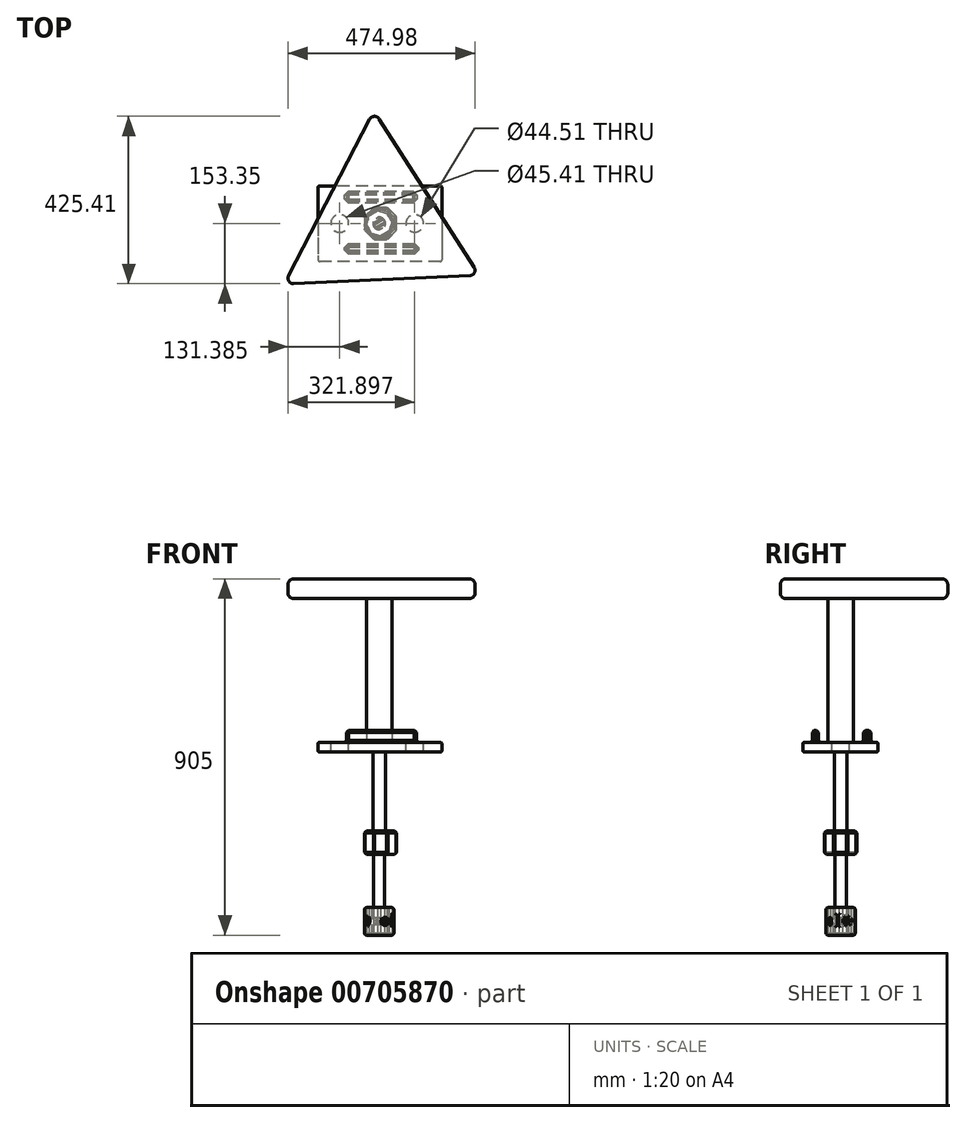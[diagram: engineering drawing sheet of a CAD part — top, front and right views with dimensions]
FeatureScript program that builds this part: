
annotation { "Feature Type Name" : "Feature", "Feature Type Description" : "" }
export const myFeature = defineFeature(function(context is Context, id is Id, definition is map)
    precondition{}
    {
        {
            var Q0;
            Q0=qCreatedBy(makeId("Top.planeOp"),FACE);
            var sketch = newSketch(context, id + "F0", { "sketchPlane" : qUnion([Q0])});
            skCircle(sketch, "E0.cCircle", {"center": v(0, 0) * mm, "radius": 34.9 * mm, "construction": true});
            skLineSegment(sketch, "E0.0", {"start": v(23.22, 29.8) * mm, "end": v(37.49, 4.65) * mm});
            skLineSegment(sketch, "E0.1", {"start": v(37.49, 4.65) * mm, "end": v(29.8, -23.22) * mm});
            skLineSegment(sketch, "E0.2", {"start": v(29.8, -23.22) * mm, "end": v(4.65, -37.49) * mm});
            skLineSegment(sketch, "E0.3", {"start": v(4.65, -37.49) * mm, "end": v(-23.22, -29.8) * mm});
            skLineSegment(sketch, "E0.4", {"start": v(-23.22, -29.8) * mm, "end": v(-37.49, -4.65) * mm});
            skLineSegment(sketch, "E0.5", {"start": v(-37.49, -4.65) * mm, "end": v(-29.8, 23.22) * mm});
            skLineSegment(sketch, "E0.6", {"start": v(-29.8, 23.22) * mm, "end": v(-4.65, 37.49) * mm});
            skLineSegment(sketch, "E0.7", {"start": v(-4.65, 37.49) * mm, "end": v(23.22, 29.8) * mm});
            skPoint(sketch, "E0.0.midPoint", {"position": v(30.35, 17.23) * mm});
            skSolve(sketch);
        }
        {
            var Q0;
            Q0 = qSketchRegion(id + "F0", true);
            extrude(context, id + "F1", {"entities" : qUnion([Q0]), "depth" : 70 * mm, "offsetDistance" : 25 * mm});
        }
        {
            var Q0;
            Q0=makeQuery(id+"F1.opExtrude","CAP_FACE",FACE,{"disambiguationData":[OSD([sQuery(id+"F0.wireOp",EDGE,"E0.0"),sQuery(id+"F0.wireOp",EDGE,"E0.1"),sQuery(id+"F0.wireOp",EDGE,"E0.2"),sQuery(id+"F0.wireOp",EDGE,"E0.3"),sQuery(id+"F0.wireOp",EDGE,"E0.4"),sQuery(id+"F0.wireOp",EDGE,"E0.5"),sQuery(id+"F0.wireOp",EDGE,"E0.6"),sQuery(id+"F0.wireOp",EDGE,"E0.7")])],"isStart":false});
            shell(context, id + "F2", {"entities" : qUnion([Q0]), "thickness" : 5 * mm});
        }
        {
            var Q0;
            Q0=makeQuery(id+"F1.opExtrude","SWEPT_FACE",FACE,{"disambiguationData":[OSD([sQuery(id+"F0.wireOp",EDGE,"E0.2")])]});
            var sketch = newSketch(context, id + "F3", { "sketchPlane" : qUnion([Q0])});
            skCircle(sketch, "E1", {"center": v(0, 34.96) * mm, "radius": 10.52 * mm});
            skSolve(sketch);
        }
        {
            var Q0;
            Q0 = qSketchRegion(id + "F3", true);
            extrude(context, id + "F4", {"entities" : qUnion([Q0]), "operationType" : NewBodyOperationType.REMOVE, "oppositeDirection" : true, "depth" : 72.7 * mm, "offsetDistance" : 25 * mm});
        }
        {
            var Q0;
            Q0=makeQuery(id+"F1.opExtrude","SWEPT_FACE",FACE,{"disambiguationData":[OSD([sQuery(id+"F0.wireOp",EDGE,"E0.1")])]});
            var sketch = newSketch(context, id + "F5", { "sketchPlane" : qUnion([Q0])});
            skLineSegment(sketch, "E2.bottom", {"start": v(0, 25.22) * mm, "end": v(2.73, 25.22) * mm});
            skLineSegment(sketch, "E2.top", {"start": v(0, 49.95) * mm, "end": v(2.73, 49.95) * mm});
            skLineSegment(sketch, "E2.left", {"start": v(0, 25.22) * mm, "end": v(0, 49.95) * mm});
            skLineSegment(sketch, "E2.right", {"start": v(2.73, 25.22) * mm, "end": v(2.73, 49.95) * mm});
            skSolve(sketch);
        }
        {
            var Q0;
            Q0 = qSketchRegion(id + "F5", true);
            extrude(context, id + "F6", {"entities" : qUnion([Q0]), "operationType" : NewBodyOperationType.REMOVE, "oppositeDirection" : true, "depth" : 81.6 * mm, "offsetDistance" : 25 * mm});
        }
        {
            var Q0;
            Q0=makeQuery(id+"F2.opShell","OFFSET_FACE",FACE,{"disambiguationData":[OSD([sQuery(id+"F0.wireOp",EDGE,"E0.0"),sQuery(id+"F0.wireOp",EDGE,"E0.1"),sQuery(id+"F0.wireOp",EDGE,"E0.2"),sQuery(id+"F0.wireOp",EDGE,"E0.3"),sQuery(id+"F0.wireOp",EDGE,"E0.4"),sQuery(id+"F0.wireOp",EDGE,"E0.5"),sQuery(id+"F0.wireOp",EDGE,"E0.6"),sQuery(id+"F0.wireOp",EDGE,"E0.7")])]});
            var sketch = newSketch(context, id + "F7", { "sketchPlane" : qUnion([Q0])});
            skCircle(sketch, "E3", {"center": v(0, 0) * mm, "radius": 14.1 * mm});
            skSolve(sketch);
        }
        {
            var Q0;
            Q0 = qSketchRegion(id + "F7", true);
            extrude(context, id + "F8", {"entities" : qUnion([Q0]), "operationType" : NewBodyOperationType.ADD, "depth" : 200 * mm, "offsetDistance" : 25 * mm});
        }
        {
            var Q0;
            Q0=makeQuery(id+"F1.opExtrude","SWEPT_FACE",FACE,{"disambiguationData":[OSD([sQuery(id+"F0.wireOp",EDGE,"E0.0")])]});
            var sketch = newSketch(context, id + "F9", { "sketchPlane" : qUnion([Q0])});
            skCircle(sketch, "E4.cCircle", {"center": v(0, 36.54) * mm, "radius": 7.96 * mm, "construction": true});
            skLineSegment(sketch, "E4.0", {"start": v(-3.31, 27.96) * mm, "end": v(-9.08, 35.12) * mm});
            skLineSegment(sketch, "E4.1", {"start": v(-9.08, 35.12) * mm, "end": v(-5.77, 43.7) * mm});
            skLineSegment(sketch, "E4.2", {"start": v(-5.77, 43.7) * mm, "end": v(3.31, 45.12) * mm});
            skLineSegment(sketch, "E4.3", {"start": v(3.31, 45.12) * mm, "end": v(9.08, 37.96) * mm});
            skLineSegment(sketch, "E4.4", {"start": v(9.08, 37.96) * mm, "end": v(5.77, 29.39) * mm});
            skLineSegment(sketch, "E4.5", {"start": v(5.77, 29.39) * mm, "end": v(-3.31, 27.96) * mm});
            skPoint(sketch, "E4.0.midPoint", {"position": v(-6.2, 31.54) * mm});
            skSolve(sketch);
        }
        {
            var Q0;
            Q0 = qSketchRegion(id + "F9", true);
            extrude(context, id + "F10", {"entities" : qUnion([Q0]), "operationType" : NewBodyOperationType.REMOVE, "oppositeDirection" : true, "depth" : 96 * mm, "offsetDistance" : 25 * mm});
        }
        {
            var Q0;
            Q0=makeQuery(id+"F8.opExtrude","CAP_FACE",FACE,{"disambiguationData":[OSD([sQuery(id+"F7.wireOp",EDGE,"E3")])],"isStart":false});
            var sketch = newSketch(context, id + "F11", { "sketchPlane" : qUnion([Q0])});
            skCircle(sketch, "E5.cCircle", {"center": v(3.58, 0) * mm, "radius": 40.85 * mm, "construction": true});
            skLineSegment(sketch, "E5.0", {"start": v(20.5, -40.85) * mm, "end": v(-13.34, -40.85) * mm});
            skLineSegment(sketch, "E5.1", {"start": v(-13.34, -40.85) * mm, "end": v(-37.27, -16.92) * mm});
            skLineSegment(sketch, "E5.2", {"start": v(-37.27, -16.92) * mm, "end": v(-37.27, 16.92) * mm});
            skLineSegment(sketch, "E5.3", {"start": v(-37.27, 16.92) * mm, "end": v(-13.34, 40.85) * mm});
            skLineSegment(sketch, "E5.4", {"start": v(-13.34, 40.85) * mm, "end": v(20.5, 40.85) * mm});
            skLineSegment(sketch, "E5.5", {"start": v(20.5, 40.85) * mm, "end": v(44.43, 16.92) * mm});
            skLineSegment(sketch, "E5.6", {"start": v(44.43, 16.92) * mm, "end": v(44.43, -16.92) * mm});
            skLineSegment(sketch, "E5.7", {"start": v(44.43, -16.92) * mm, "end": v(20.5, -40.85) * mm});
            skPoint(sketch, "E5.0.midPoint", {"position": v(3.58, -40.85) * mm});
            skSolve(sketch);
        }
        {
            var Q0;
            Q0 = qSketchRegion(id + "F11", true);
            extrude(context, id + "F12", {"entities" : qUnion([Q0]), "operationType" : NewBodyOperationType.ADD, "depth" : 60 * mm, "offsetDistance" : 25 * mm});
        }
        {
            var Q0;
            Q0=makeQuery(id+"F12.opExtrude","CAP_EDGE",EDGE,{"disambiguationData":[OSD([sQuery(id+"F11.wireOp",EDGE,"E5.7")])],"isStart":false});
            var Q1;
            Q1=makeQuery(id+"F12.opExtrude","CAP_EDGE",EDGE,{"disambiguationData":[OSD([sQuery(id+"F11.wireOp",EDGE,"E5.6")])],"isStart":false});
            var Q2;
            Q2=makeQuery(id+"F12.opExtrude","CAP_EDGE",EDGE,{"disambiguationData":[OSD([sQuery(id+"F11.wireOp",EDGE,"E5.5")])],"isStart":false});
            var Q3;
            Q3=makeQuery(id+"F12.opExtrude","CAP_EDGE",EDGE,{"disambiguationData":[OSD([sQuery(id+"F11.wireOp",EDGE,"E5.4")])],"isStart":false});
            var Q4;
            Q4=makeQuery(id+"F12.opExtrude","CAP_EDGE",EDGE,{"disambiguationData":[OSD([sQuery(id+"F11.wireOp",EDGE,"E5.3")])],"isStart":false});
            var Q5;
            Q5=makeQuery(id+"F12.opExtrude","CAP_EDGE",EDGE,{"disambiguationData":[OSD([sQuery(id+"F11.wireOp",EDGE,"E5.2")])],"isStart":false});
            var Q6;
            Q6=makeQuery(id+"F12.opExtrude","CAP_EDGE",EDGE,{"disambiguationData":[OSD([sQuery(id+"F11.wireOp",EDGE,"E5.1")])],"isStart":false});
            var Q7;
            Q7=makeQuery(id+"F12.opExtrude","CAP_EDGE",EDGE,{"disambiguationData":[OSD([sQuery(id+"F11.wireOp",EDGE,"E5.0")])],"isStart":false});
            var Q8;
            Q8=makeQuery(id+"F12.opExtrude","SWEPT_FACE",FACE,{"disambiguationData":[OSD([sQuery(id+"F11.wireOp",EDGE,"E5.4")])]});
            var Q9;
            Q9=makeQuery(id+"F12.opExtrude","SWEPT_FACE",FACE,{"disambiguationData":[OSD([sQuery(id+"F11.wireOp",EDGE,"E5.3")])]});
            var Q10;
            Q10=makeQuery(id+"F12.opExtrude","SWEPT_FACE",FACE,{"disambiguationData":[OSD([sQuery(id+"F11.wireOp",EDGE,"E5.2")])]});
            var Q11;
            Q11=makeQuery(id+"F12.opExtrude","SWEPT_FACE",FACE,{"disambiguationData":[OSD([sQuery(id+"F11.wireOp",EDGE,"E5.1")])]});
            var Q12;
            Q12=makeQuery(id+"F12.opExtrude","SWEPT_FACE",FACE,{"disambiguationData":[OSD([sQuery(id+"F11.wireOp",EDGE,"E5.0")])]});
            var Q13;
            Q13=makeQuery(id+"F12.opExtrude","SWEPT_FACE",FACE,{"disambiguationData":[OSD([sQuery(id+"F11.wireOp",EDGE,"E5.6")])]});
            chamfer(context, id + "F13", {"entities" : qUnion([Q0, Q1, Q2, Q3, Q4, Q5, Q6, Q7, Q8, Q9, Q10, Q11, Q12, Q13]), "width" : 5 * mm, "tangentPropagation" : true});
        }
        {
            var Q0;
            Q0=makeQuery(id+"F1.opExtrude","SWEPT_FACE",FACE,{"disambiguationData":[OSD([sQuery(id+"F0.wireOp",EDGE,"E0.4")])]});
            var Q1;
            Q1=makeQuery(id+"F1.opExtrude","SWEPT_FACE",FACE,{"disambiguationData":[OSD([sQuery(id+"F0.wireOp",EDGE,"E0.5")])]});
            var Q2;
            Q2=makeQuery(id+"F1.opExtrude","SWEPT_FACE",FACE,{"disambiguationData":[OSD([sQuery(id+"F0.wireOp",EDGE,"E0.6")])]});
            var Q3;
            Q3=makeQuery(id+"F1.opExtrude","SWEPT_FACE",FACE,{"disambiguationData":[OSD([sQuery(id+"F0.wireOp",EDGE,"E0.7")])]});
            var Q4;
            Q4=makeQuery(id+"F1.opExtrude","SWEPT_FACE",FACE,{"disambiguationData":[OSD([sQuery(id+"F0.wireOp",EDGE,"E0.0")])]});
            var Q5;
            Q5=makeQuery(id+"F1.opExtrude","SWEPT_FACE",FACE,{"disambiguationData":[OSD([sQuery(id+"F0.wireOp",EDGE,"E0.1")])]});
            var Q6;
            Q6=makeQuery(id+"F1.opExtrude","SWEPT_FACE",FACE,{"disambiguationData":[OSD([sQuery(id+"F0.wireOp",EDGE,"E0.2")])]});
            var Q7;
            Q7=makeQuery(id+"F1.opExtrude","SWEPT_FACE",FACE,{"disambiguationData":[OSD([sQuery(id+"F0.wireOp",EDGE,"E0.3")])]});
            fillet(context, id + "F14", {"entities" : qUnion([Q0, Q1, Q2, Q3, Q4, Q5, Q6, Q7]), "radius" : 5 * mm, "tangentPropagation" : true, "allowEdgeOverflow" : false});
        }
        {
            var Q0;
            Q0=makeQuery(id+"F12.opExtrude","CAP_FACE",FACE,{"disambiguationData":[OSD([sQuery(id+"F11.wireOp",EDGE,"E5.0"),sQuery(id+"F11.wireOp",EDGE,"E5.1"),sQuery(id+"F11.wireOp",EDGE,"E5.2"),sQuery(id+"F11.wireOp",EDGE,"E5.3"),sQuery(id+"F11.wireOp",EDGE,"E5.4"),sQuery(id+"F11.wireOp",EDGE,"E5.5"),sQuery(id+"F11.wireOp",EDGE,"E5.6"),sQuery(id+"F11.wireOp",EDGE,"E5.7")])],"isStart":false});
            var sketch = newSketch(context, id + "F15", { "sketchPlane" : qUnion([Q0])});
            skCircle(sketch, "E6", {"center": v(0, 0) * mm, "radius": 16.04 * mm});
            skSolve(sketch);
        }
        {
            var Q0;
            Q0 = qSketchRegion(id + "F15", true);
            extrude(context, id + "F16", {"entities" : qUnion([Q0]), "operationType" : NewBodyOperationType.ADD, "depth" : 200 * mm, "offsetDistance" : 25 * mm});
        }
        {
            var Q0;
            Q0=makeQuery(id+"F16.opExtrude","CAP_FACE",FACE,{"disambiguationData":[OSD([sQuery(id+"F15.wireOp",EDGE,"E6")])],"isStart":false});
            var sketch = newSketch(context, id + "F17", { "sketchPlane" : qUnion([Q0])});
            skLineSegment(sketch, "E7.bottom", {"start": v(159.79, 95.16) * mm, "end": v(-155.8, 95.16) * mm});
            skLineSegment(sketch, "E7.top", {"start": v(159.79, -96.44) * mm, "end": v(-155.8, -96.44) * mm});
            skLineSegment(sketch, "E7.left", {"start": v(159.79, 95.16) * mm, "end": v(159.79, -96.44) * mm});
            skLineSegment(sketch, "E7.right", {"start": v(-155.8, 95.16) * mm, "end": v(-155.8, -96.44) * mm});
            skSolve(sketch);
        }
        {
            var Q0;
            Q0 = qSketchRegion(id + "F17", true);
            extrude(context, id + "F18", {"entities" : qUnion([Q0]), "operationType" : NewBodyOperationType.ADD, "depth" : 25 * mm, "offsetDistance" : 25 * mm});
        }
        {
            var Q0;
            Q0=makeQuery(id+"F18.opExtrude","CAP_FACE",FACE,{"disambiguationData":[OSD([sQuery(id+"F17.wireOp",EDGE,"E7.bottom"),sQuery(id+"F17.wireOp",EDGE,"E7.top"),sQuery(id+"F17.wireOp",EDGE,"E7.left"),sQuery(id+"F17.wireOp",EDGE,"E7.right")])],"isStart":false});
            var sketch = newSketch(context, id + "F19", { "sketchPlane" : qUnion([Q0])});
            skCircle(sketch, "E8", {"center": v(-100.14, 0) * mm, "radius": 22.7 * mm});
            skCircle(sketch, "E9", {"center": v(90.37, 0) * mm, "radius": 22.25 * mm});
            skSolve(sketch);
        }
        {
            var Q0;
            Q0 = qSketchRegion(id + "F19", true);
            extrude(context, id + "F20", {"entities" : qUnion([Q0]), "operationType" : NewBodyOperationType.REMOVE, "oppositeDirection" : true, "depth" : 73 * mm, "offsetDistance" : 25 * mm});
        }
        {
            var Q0;
            Q0=makeQuery(id+"F18.opExtrude","CAP_EDGE",EDGE,{"disambiguationData":[OSD([sQuery(id+"F17.wireOp",EDGE,"E7.right")])],"isStart":false});
            var Q1;
            Q1=makeQuery(id+"F18.opExtrude","CAP_EDGE",EDGE,{"disambiguationData":[OSD([sQuery(id+"F17.wireOp",EDGE,"E7.bottom")])],"isStart":false});
            var Q2;
            Q2=makeQuery(id+"F18.opExtrude","CAP_EDGE",EDGE,{"disambiguationData":[OSD([sQuery(id+"F17.wireOp",EDGE,"E7.left")])],"isStart":false});
            var Q3;
            Q3=makeQuery(id+"F18.opExtrude","CAP_EDGE",EDGE,{"disambiguationData":[OSD([sQuery(id+"F17.wireOp",EDGE,"E7.top")])],"isStart":false});
            var Q4;
            Q4=makeQuery(id+"F20.boolean.opBoolean","COPY",EDGE,{"derivedFrom":makeQuery(id+"F20.opExtrude","CAP_EDGE",EDGE,{"disambiguationData":[OSD([sQuery(id+"F19.wireOp",EDGE,"E8")])],"isStart":true})});
            var Q5;
            Q5=makeQuery(id+"F20.boolean.opBoolean","COPY",EDGE,{"derivedFrom":makeQuery(id+"F20.opExtrude","CAP_EDGE",EDGE,{"disambiguationData":[OSD([sQuery(id+"F19.wireOp",EDGE,"E9")])],"isStart":true})});
            fillet(context, id + "F21", {"entities" : qUnion([Q0, Q1, Q2, Q3, Q4, Q5]), "radius" : 5 * mm, "tangentPropagation" : true, "allowEdgeOverflow" : false});
        }
        {
            var Q0;
            Q0=makeQuery(id+"F18.opExtrude","SWEPT_FACE",FACE,{"disambiguationData":[OSD([sQuery(id+"F17.wireOp",EDGE,"E7.top")])]});
            var Q1;
            Q1=makeQuery(id+"F18.opExtrude","SWEPT_FACE",FACE,{"disambiguationData":[OSD([sQuery(id+"F17.wireOp",EDGE,"E7.right")])]});
            var Q2;
            Q2=makeQuery(id+"F18.opExtrude","SWEPT_FACE",FACE,{"disambiguationData":[OSD([sQuery(id+"F17.wireOp",EDGE,"E7.bottom")])]});
            var Q3;
            Q3=makeQuery(id+"F18.opExtrude","CAP_EDGE",EDGE,{"disambiguationData":[OSD([sQuery(id+"F17.wireOp",EDGE,"E7.left")])],"isStart":true});
            var Q4;
            {var subQ0=sQuery(id+"F19.wireOp",EDGE,"E9");Q4=makeQuery(id+"F21.opFillet","BLEND_EDGE",EDGE,{"blendedFrom":[makeQuery(id+"F20.boolean.opBoolean","COPY",EDGE,{"derivedFrom":makeQuery(id+"F20.opExtrude","CAP_EDGE",EDGE,{"disambiguationData":[OSD([subQ0])],"isStart":true})}),makeQuery(id+"F20.boolean.opBoolean","COPY",FACE,{"derivedFrom":makeQuery(id+"F20.opExtrude","SWEPT_FACE",FACE,{"disambiguationData":[OSD([subQ0])]})})],"blendedInto":[makeQuery(id+"F20.boolean.opBoolean","COPY",FACE,{"derivedFrom":makeQuery(id+"F20.opExtrude","SWEPT_FACE",FACE,{"disambiguationData":[OSD([subQ0])]})})]});}
            var Q5;
            Q5=makeQuery(id+"F20.boolean.opBoolean","COPY",FACE,{"derivedFrom":makeQuery(id+"F20.opExtrude","SWEPT_FACE",FACE,{"disambiguationData":[OSD([sQuery(id+"F19.wireOp",EDGE,"E8")])]})});
            var Q6;
            Q6=makeQuery(id+"F20.boolean.opBoolean","INTERSECT",EDGE,{"derivedFrom":[makeQuery(id+"F18.opExtrude","CAP_FACE",FACE,{"disambiguationData":[OSD([sQuery(id+"F17.wireOp",EDGE,"E7.bottom"),sQuery(id+"F17.wireOp",EDGE,"E7.top"),sQuery(id+"F17.wireOp",EDGE,"E7.left"),sQuery(id+"F17.wireOp",EDGE,"E7.right")])],"isStart":true}),makeQuery(id+"F20.opExtrude","SWEPT_FACE",FACE,{"disambiguationData":[OSD([sQuery(id+"F19.wireOp",EDGE,"E9")])]})]});
            fillet(context, id + "F22", {"entities" : qUnion([Q0, Q1, Q2, Q3, Q4, Q5, Q6]), "radius" : 5 * mm, "tangentPropagation" : true, "allowEdgeOverflow" : false});
        }
        {
            var Q0;
            Q0=makeQuery(id+"F18.opExtrude","CAP_FACE",FACE,{"disambiguationData":[OSD([sQuery(id+"F17.wireOp",EDGE,"E7.bottom"),sQuery(id+"F17.wireOp",EDGE,"E7.top"),sQuery(id+"F17.wireOp",EDGE,"E7.left"),sQuery(id+"F17.wireOp",EDGE,"E7.right")])],"isStart":false});
            var sketch = newSketch(context, id + "F23", { "sketchPlane" : qUnion([Q0])});
            skLineSegment(sketch, "E10.bottom", {"start": v(-83.04, 76.87) * mm, "end": v(91.23, 76.87) * mm});
            skLineSegment(sketch, "E10.top", {"start": v(-83.04, 57.3) * mm, "end": v(91.23, 57.3) * mm});
            skLineSegment(sketch, "E10.left", {"start": v(-83.04, 76.87) * mm, "end": v(-83.04, 57.3) * mm});
            skLineSegment(sketch, "E10.right", {"start": v(91.23, 76.87) * mm, "end": v(91.23, 57.3) * mm});
            skLineSegment(sketch, "E11.bottom", {"start": v(-83.04, -55.88) * mm, "end": v(94.75, -55.88) * mm});
            skLineSegment(sketch, "E11.top", {"start": v(-83.04, -72.33) * mm, "end": v(94.75, -72.33) * mm});
            skLineSegment(sketch, "E11.left", {"start": v(-83.04, -55.88) * mm, "end": v(-83.04, -72.33) * mm});
            skLineSegment(sketch, "E11.right", {"start": v(94.75, -55.88) * mm, "end": v(94.75, -72.33) * mm});
            skSolve(sketch);
        }
        {
            var Q0;
            Q0=makeQuery(id+"F23.imprint","IMPRINT",FACE,{"disambiguationData":[TD([[makeQuery(id+"F23.imprint","IMPRINT",EDGE,{"derivedFrom":sQuery(id+"F23.wireOp",EDGE,"E11.bottom")}),-1.0]])]});
            var Q1;
            Q1=makeQuery(id+"F23.imprint","IMPRINT",FACE,{"disambiguationData":[TD([[makeQuery(id+"F23.imprint","IMPRINT",EDGE,{"derivedFrom":sQuery(id+"F23.wireOp",EDGE,"E10.bottom")}),-1.0]])]});
            extrude(context, id + "F24", {"entities" : qUnion([Q0, Q1]), "operationType" : NewBodyOperationType.ADD, "depth" : 30 * mm, "offsetDistance" : 25 * mm});
        }
        {
            var Q0;
            Q0=makeQuery(id+"F24.opExtrude","CAP_FACE",FACE,{"disambiguationData":[OSD([sQuery(id+"F23.wireOp",EDGE,"E10.bottom"),sQuery(id+"F23.wireOp",EDGE,"E10.top"),sQuery(id+"F23.wireOp",EDGE,"E10.left"),sQuery(id+"F23.wireOp",EDGE,"E10.right")])],"isStart":false});
            var Q1;
            Q1=makeQuery(id+"F24.opExtrude","CAP_FACE",FACE,{"disambiguationData":[OSD([sQuery(id+"F23.wireOp",EDGE,"E11.bottom"),sQuery(id+"F23.wireOp",EDGE,"E11.top"),sQuery(id+"F23.wireOp",EDGE,"E11.left"),sQuery(id+"F23.wireOp",EDGE,"E11.right")])],"isStart":false});
            var Q2;
            Q2=makeQuery(id+"F24.opExtrude","SWEPT_FACE",FACE,{"disambiguationData":[OSD([sQuery(id+"F23.wireOp",EDGE,"E11.top")])]});
            var Q3;
            Q3=makeQuery(id+"F24.opExtrude","SWEPT_FACE",FACE,{"disambiguationData":[OSD([sQuery(id+"F23.wireOp",EDGE,"E11.bottom")])]});
            var Q4;
            Q4=makeQuery(id+"F24.opExtrude","SWEPT_FACE",FACE,{"disambiguationData":[OSD([sQuery(id+"F23.wireOp",EDGE,"E10.bottom")])]});
            var Q5;
            Q5=makeQuery(id+"F24.opExtrude","SWEPT_FACE",FACE,{"disambiguationData":[OSD([sQuery(id+"F23.wireOp",EDGE,"E10.top")])]});
            chamfer(context, id + "F25", {"entities" : qUnion([Q0, Q1, Q2, Q3, Q4, Q5]), "width" : 5 * mm, "tangentPropagation" : true});
        }
        {
            var Q0;
            Q0=makeQuery(id+"F18.opExtrude","CAP_FACE",FACE,{"disambiguationData":[OSD([sQuery(id+"F17.wireOp",EDGE,"E7.bottom"),sQuery(id+"F17.wireOp",EDGE,"E7.top"),sQuery(id+"F17.wireOp",EDGE,"E7.left"),sQuery(id+"F17.wireOp",EDGE,"E7.right")])],"isStart":false});
            var sketch = newSketch(context, id + "F26", { "sketchPlane" : qUnion([Q0])});
            skCircle(sketch, "E12", {"center": v(0, 0) * mm, "radius": 32.48 * mm});
            skSolve(sketch);
        }
        {
            var Q0;
            Q0 = qSketchRegion(id + "F26", true);
            extrude(context, id + "F27", {"entities" : qUnion([Q0]), "operationType" : NewBodyOperationType.ADD, "depth" : 365 * mm, "offsetDistance" : 25 * mm});
        }
        {
            var Q0;
            Q0=makeQuery(id+"F27.opExtrude","CAP_FACE",FACE,{"disambiguationData":[OSD([sQuery(id+"F26.wireOp",EDGE,"E12")])],"isStart":false});
            var sketch = newSketch(context, id + "F28", { "sketchPlane" : qUnion([Q0])});
            skCircle(sketch, "E13.cCircle", {"center": v(0, 0) * mm, "radius": 143.17 * mm, "construction": true});
            skLineSegment(sketch, "E13.0", {"start": v(-13.2, 286.03) * mm, "end": v(254.32, -131.58) * mm});
            skLineSegment(sketch, "E13.1", {"start": v(254.32, -131.58) * mm, "end": v(-241.1, -154.45) * mm});
            skLineSegment(sketch, "E13.2", {"start": v(-241.1, -154.45) * mm, "end": v(-13.2, 286.03) * mm});
            skPoint(sketch, "E13.0.midPoint", {"position": v(120.55, 77.23) * mm});
            skSolve(sketch);
        }
        {
            var Q0;
            Q0 = qSketchRegion(id + "F28", true);
            extrude(context, id + "F29", {"entities" : qUnion([Q0]), "operationType" : NewBodyOperationType.ADD, "depth" : 50 * mm, "offsetDistance" : 25 * mm});
        }
        {
            var Q0;
            Q0=makeQuery(id+"F29.opExtrude","SWEPT_FACE",FACE,{"disambiguationData":[OSD([sQuery(id+"F28.wireOp",EDGE,"E13.0")])]});
            var Q1;
            Q1=makeQuery(id+"F29.opExtrude","SWEPT_FACE",FACE,{"disambiguationData":[OSD([sQuery(id+"F28.wireOp",EDGE,"E13.2")])]});
            var Q2;
            Q2=makeQuery(id+"F29.opExtrude","SWEPT_FACE",FACE,{"disambiguationData":[OSD([sQuery(id+"F28.wireOp",EDGE,"E13.1")])]});
            fillet(context, id + "F30", {"entities" : qUnion([Q0, Q1, Q2]), "radius" : 14 * mm, "tangentPropagation" : true, "allowEdgeOverflow" : false});
        }
    });
